MODEL slx_f09b170d5c8a
CONFIG AbsTol = auto
CONFIG FixedStep = 0.001
CONFIG MaxStep = auto
CONFIG MinStep = auto
CONFIG RelTol = 1e-3
CONFIG SampleTimeConstraint = Unconstrained
CONFIG Solver = ode5
CONFIG SolverMode = Auto
CONFIG SolverName = ode5
CONFIG StartTime = 0.0
CONFIG StopTime = 15
BLOCK [SubSystem] Control
  Ports = [3, 1]
  RequestExecContextInheritance = off
BLOCK [Constant] Control/Constant
  Value = a
BLOCK [Constant] Control/Constant1
  Value = d
BLOCK [SubSystem] Control/MATLAB Function
  ErrorFcn = Stateflow.Translate.translate
  PermitHierarchicalResolution = ExplicitOnly
  Ports = [4, 1]
  RequestExecContextInheritance = off
  SFBlockType = MATLAB Function
  TreatAsAtomicUnit = on
BLOCK [Demux] Control/MATLAB Function/ Demux 
  Outputs = 1
  Ports = [1, 1]
BLOCK [S-Function] Control/MATLAB Function/ SFunction 
  EnableBusSupport = on
  FunctionName = sf_sfun
  PortCounts = [4 2]
  Ports = [4, 2]
  Tag = Stateflow S-Function Static 2
BLOCK [Terminator] Control/MATLAB Function/ Terminator 
BLOCK [Outport] Control/MATLAB Function/K_inv
  IconDisplay = Port number
BLOCK [Inport] Control/MATLAB Function/a
  IconDisplay = Port number
  Port = 3
BLOCK [Inport] Control/MATLAB Function/beta
  IconDisplay = Port number
  Port = 2
BLOCK [Inport] Control/MATLAB Function/d
  IconDisplay = Port number
  Port = 4
BLOCK [Inport] Control/MATLAB Function/theta
  IconDisplay = Port number
BLOCK [Product] Control/Product
  InputSameDT = off
  Multiplication = Matrix(*)
  OutDataTypeStr = Inherit: Inherit via internal rule
  Ports = [2, 1]
  RndMeth = Floor
  SaturateOnIntegerOverflow = off
BLOCK [Inport] Control/W
  IconDisplay = Port number
BLOCK [Inport] Control/beta
  IconDisplay = Port number
  Port = 3
BLOCK [Inport] Control/theta
  IconDisplay = Port number
  Port = 2
BLOCK [Outport] Control/u
  IconDisplay = Port number
BLOCK [SubSystem] DKM
  Ports = [1, 4]
  RequestExecContextInheritance = off
BLOCK [Constant] DKM/Constant
  Value = r
BLOCK [Constant] DKM/Constant1
  Value = a
BLOCK [Demux] DKM/Demux1
  DisplayOption = bar
  Outputs = 2
  Ports = [1, 2]
BLOCK [Fcn] DKM/Fcn1
  Expr = sin(u)
BLOCK [Integrator] DKM/Integrator
  Ports = [1, 1]
BLOCK [Integrator] DKM/Integrator2
  InitialCondition = theta0
  Ports = [1, 1]
BLOCK [SubSystem] DKM/MATLAB Function2
  ErrorFcn = Stateflow.Translate.translate
  PermitHierarchicalResolution = ExplicitOnly
  Ports = [4, 2]
  RequestExecContextInheritance = off
  SFBlockType = MATLAB Function
  TreatAsAtomicUnit = on
BLOCK [Demux] DKM/MATLAB Function2/ Demux 
  Outputs = 1
  Ports = [1, 1]
BLOCK [S-Function] DKM/MATLAB Function2/ SFunction 
  EnableBusSupport = on
  FunctionName = sf_sfun
  PortCounts = [4 3]
  Ports = [4, 3]
  Tag = Stateflow S-Function Static 4
BLOCK [Terminator] DKM/MATLAB Function2/ Terminator 
BLOCK [Inport] DKM/MATLAB Function2/a
  IconDisplay = Port number
  Port = 2
BLOCK [Inport] DKM/MATLAB Function2/beta
  IconDisplay = Port number
  Port = 3
BLOCK [Inport] DKM/MATLAB Function2/theta
  IconDisplay = Port number
  Port = 4
BLOCK [Inport] DKM/MATLAB Function2/u_m
  IconDisplay = Port number
BLOCK [Outport] DKM/MATLAB Function2/x_dot
  IconDisplay = Port number
BLOCK [Outport] DKM/MATLAB Function2/y_dot
  IconDisplay = Port number
  Port = 2
BLOCK [Mux] DKM/Mux
  DisplayOption = bar
  Inputs = 2
  Ports = [2, 1]
BLOCK [Product] DKM/Product
  InputSameDT = off
  Inputs = **/
  OutDataTypeStr = Inherit: Inherit via internal rule
  Ports = [3, 1]
  RndMeth = Floor
  SaturateOnIntegerOverflow = off
BLOCK [Product] DKM/Product1
  InputSameDT = off
  OutDataTypeStr = Inherit: Inherit via internal rule
  Ports = [2, 1]
  RndMeth = Floor
  SaturateOnIntegerOverflow = off
BLOCK [ToWorkspace] DKM/To Workspace
  FixptAsFi = on
  MaxDataPoints = inf
  Ports = [1]
  SampleTime = -1
  Save2DSignal = 3-D array (concatenate along third dimension)
  VariableName = u
BLOCK [Outport] DKM/beta
  IconDisplay = Port number
  Port = 4
BLOCK [Inport] DKM/q_dot
  IconDisplay = Port number
BLOCK [Outport] DKM/theta
  IconDisplay = Port number
  Port = 3
BLOCK [Outport] DKM/x_dot
  IconDisplay = Port number
BLOCK [Outport] DKM/y_dot
  IconDisplay = Port number
  Port = 2
BLOCK [Gain] Gain
  Gain = K
  OutDataTypeStr = Inherit: Inherit via internal rule
  ParamDataTypeStr = Inherit: Inherit via internal rule
  SaturateOnIntegerOverflow = off
BLOCK [SubSystem] IKM
  Ports = [1, 1]
  RequestExecContextInheritance = off
BLOCK [Constant] IKM/Constant
  Value = a_e
BLOCK [Constant] IKM/Constant1
  Value = r_e
BLOCK [Demux] IKM/Demux
  DisplayOption = bar
  Outputs = 2
  Ports = [1, 2]
BLOCK [Mux] IKM/Mux
  DisplayOption = bar
  Inputs = 2
  Ports = [2, 1]
BLOCK [Product] IKM/Product
  InputSameDT = off
  Inputs = **/
  OutDataTypeStr = Inherit: Inherit via internal rule
  Ports = [3, 1]
  RndMeth = Floor
  SaturateOnIntegerOverflow = off
BLOCK [Outport] IKM/q_dot
  IconDisplay = Port number
BLOCK [Inport] IKM/u
  IconDisplay = Port number
BLOCK [SubSystem] Localization
  Ports = [4, 1]
  RequestExecContextInheritance = off
BLOCK [Constant] Localization/Constant1
  Value = a
BLOCK [Constant] Localization/Constant2
  Value = d
BLOCK [Integrator] Localization/Integrator2
  InitialCondition = x0
  Ports = [1, 1]
BLOCK [Integrator] Localization/Integrator3
  InitialCondition = y0
  Ports = [1, 1]
BLOCK [SubSystem] Localization/MATLAB Function1
  ErrorFcn = Stateflow.Translate.translate
  PermitHierarchicalResolution = ExplicitOnly
  Ports = [6, 1]
  RequestExecContextInheritance = off
  SFBlockType = MATLAB Function
  TreatAsAtomicUnit = on
BLOCK [Demux] Localization/MATLAB Function1/ Demux 
  Outputs = 1
  Ports = [1, 1]
BLOCK [S-Function] Localization/MATLAB Function1/ SFunction 
  EnableBusSupport = on
  FunctionName = sf_sfun
  PortCounts = [6 2]
  Ports = [6, 2]
  Tag = Stateflow S-Function Static 3
BLOCK [Terminator] Localization/MATLAB Function1/ Terminator 
BLOCK [Inport] Localization/MATLAB Function1/a
  IconDisplay = Port number
  Port = 6
BLOCK [Inport] Localization/MATLAB Function1/beta
  IconDisplay = Port number
  Port = 3
BLOCK [Inport] Localization/MATLAB Function1/d
  IconDisplay = Port number
  Port = 5
BLOCK [Outport] Localization/MATLAB Function1/h
  IconDisplay = Port number
BLOCK [Inport] Localization/MATLAB Function1/theta
  IconDisplay = Port number
  Port = 4
BLOCK [Inport] Localization/MATLAB Function1/x
  IconDisplay = Port number
BLOCK [Inport] Localization/MATLAB Function1/y
  IconDisplay = Port number
  Port = 2
BLOCK [Mux] Localization/Mux
  DisplayOption = bar
  Inputs = 2
  Ports = [2, 1]
BLOCK [ToWorkspace] Localization/To Workspace
  FixptAsFi = on
  MaxDataPoints = inf
  Ports = [1]
  SampleTime = -1
  Save2DSignal = 3-D array (concatenate along third dimension)
  VariableName = h
BLOCK [ToWorkspace] Localization/To Workspace1
  FixptAsFi = on
  MaxDataPoints = inf
  Ports = [1]
  SampleTime = -1
  Save2DSignal = 3-D array (concatenate along third dimension)
  VariableName = beta
BLOCK [Inport] Localization/beta
  IconDisplay = Port number
  Port = 4
BLOCK [Outport] Localization/h
  IconDisplay = Port number
BLOCK [Inport] Localization/theta
  IconDisplay = Port number
  Port = 3
BLOCK [Inport] Localization/x_dot
  IconDisplay = Port number
BLOCK [Inport] Localization/y_dot
  IconDisplay = Port number
  Port = 2
BLOCK [Mux] Mux
  DisplayOption = bar
  Inputs = 2
  Ports = [2, 1]
BLOCK [Mux] Mux1
  DisplayOption = bar
  Inputs = 2
  Ports = [2, 1]
BLOCK [Sum] Sum
  IconShape = round
  InputSameDT = off
  Inputs = -+|
  OutDataTypeStr = Inherit: Inherit via internal rule
  Ports = [2, 1]
  SaturateOnIntegerOverflow = off
BLOCK [Sum] Sum1
  IconShape = round
  InputSameDT = off
  Inputs = |++
  OutDataTypeStr = Inherit: Inherit via internal rule
  Ports = [2, 1]
  SaturateOnIntegerOverflow = off
BLOCK [ToWorkspace] To Workspace2
  FixptAsFi = on
  MaxDataPoints = inf
  Ports = [1]
  SampleTime = -1
  Save2DSignal = 3-D array (concatenate along third dimension)
  VariableName = error
BLOCK [SubSystem] Trajectory Generator
  Ports = [0, 4]
  RequestExecContextInheritance = off
BLOCK [Constant] Trajectory Generator/Constant
  Value = wd
BLOCK [Constant] Trajectory Generator/Constant1
  Value = R
BLOCK [Fcn] Trajectory Generator/Fcn
  Expr = u+pi/2
BLOCK [Integrator] Trajectory Generator/Integrator
  Ports = [1, 1]
BLOCK [Mux] Trajectory Generator/Mux
  DisplayOption = bar
  Inputs = 3
  Ports = [3, 1]
BLOCK [Mux] Trajectory Generator/Mux1
  DisplayOption = bar
  Inputs = 3
  Ports = [3, 1]
BLOCK [ToWorkspace] Trajectory Generator/To Workspace
  FixptAsFi = on
  MaxDataPoints = inf
  Ports = [1]
  SampleTime = -1
  Save2DSignal = 3-D array (concatenate along third dimension)
  VariableName = hd
BLOCK [Outport] Trajectory Generator/xd
  IconDisplay = Port number
BLOCK [Fcn] Trajectory Generator/xd Func
  Expr = u(3)*cos(u(2))
BLOCK [Outport] Trajectory Generator/xd_dot
  IconDisplay = Port number
  Port = 3
BLOCK [Fcn] Trajectory Generator/xd_dot Func
  Expr = -u(3)*u(1)*sin(u(2))
BLOCK [Outport] Trajectory Generator/yd
  IconDisplay = Port number
  Port = 2
BLOCK [Fcn] Trajectory Generator/yd Func
  Expr = u(3)*sin(u(2))
BLOCK [Outport] Trajectory Generator/yd_dot
  IconDisplay = Port number
  Port = 4
BLOCK [Fcn] Trajectory Generator/yd_dot Func
  Expr = u(3)*u(1)*cos(u(2))
LINE Control/Constant1:1 -> Control/MATLAB Function:4
LINE Control/Constant:1 -> Control/MATLAB Function:3
LINE Control/MATLAB Function:1 -> Control/Product:1
LINE Control/Product:1 -> Control/u:1
LINE Control/W:1 -> Control/Product:2
LINE Control/beta:1 -> Control/MATLAB Function:2
LINE Control/theta:1 -> Control/MATLAB Function:1
LINE Control:1 -> IKM:1
LINE DKM/Constant1:1 -> DKM/MATLAB Function2:2
LINE DKM/Constant1:1 -> DKM/Product:3
LINE DKM/Constant:1 -> DKM/Product:2
LINE DKM/Demux1:1 -> DKM/Product:1
LINE DKM/Demux1:2 -> DKM/Integrator:1
LINE DKM/Demux1:2 -> DKM/Mux:2
LINE DKM/Fcn1:1 -> DKM/Product1:2
LINE DKM/Integrator2:1 -> DKM/MATLAB Function2:4
LINE DKM/Integrator2:1 -> DKM/theta:1
LINE DKM/Integrator:1 -> DKM/Fcn1:1
LINE DKM/Integrator:1 -> DKM/MATLAB Function2:3
LINE DKM/Integrator:1 -> DKM/beta:1
LINE DKM/MATLAB Function2:1 -> DKM/x_dot:1
LINE DKM/MATLAB Function2:2 -> DKM/y_dot:1
LINE DKM/Mux:1 -> DKM/To Workspace:1
LINE DKM/Product1:1 -> DKM/Integrator2:1
LINE DKM/Product:1 -> DKM/MATLAB Function2:1
LINE DKM/Product:1 -> DKM/Mux:1
LINE DKM/Product:1 -> DKM/Product1:1
LINE DKM/q_dot:1 -> DKM/Demux1:1
LINE DKM:1 -> Localization:1
LINE DKM:2 -> Localization:2
LINE DKM:3 -> Control:2
LINE DKM:3 -> Localization:3
LINE DKM:4 -> Control:3
LINE DKM:4 -> Localization:4
LINE Gain:1 -> Sum1:1
LINE IKM/Constant1:1 -> IKM/Product:3
LINE IKM/Constant:1 -> IKM/Product:1
LINE IKM/Demux:1 -> IKM/Product:2
LINE IKM/Demux:2 -> IKM/Mux:2
LINE IKM/Mux:1 -> IKM/q_dot:1
LINE IKM/Product:1 -> IKM/Mux:1
LINE IKM/u:1 -> IKM/Demux:1
LINE IKM:1 -> DKM:1
LINE Localization/Constant1:1 -> Localization/MATLAB Function1:6
LINE Localization/Constant2:1 -> Localization/MATLAB Function1:5
LINE Localization/Integrator2:1 -> Localization/MATLAB Function1:1
LINE Localization/Integrator3:1 -> Localization/MATLAB Function1:2
LINE Localization/MATLAB Function1:1 -> Localization/Mux:1
LINE Localization/MATLAB Function1:1 -> Localization/h:1
LINE Localization/Mux:1 -> Localization/To Workspace:1
LINE Localization/beta:1 -> Localization/MATLAB Function1:3
LINE Localization/beta:1 -> Localization/To Workspace1:1
LINE Localization/theta:1 -> Localization/MATLAB Function1:4
LINE Localization/theta:1 -> Localization/Mux:2
LINE Localization/x_dot:1 -> Localization/Integrator2:1
LINE Localization/y_dot:1 -> Localization/Integrator3:1
LINE Localization:1 -> Sum:1
LINE Mux1:1 -> Sum1:2
LINE Mux:1 -> Sum:2
LINE Sum1:1 -> Control:1
LINE Sum:1 -> Gain:1
LINE Sum:1 -> To Workspace2:1
LINE Trajectory Generator/Constant1:1 -> Trajectory Generator/Mux:3
LINE Trajectory Generator/Constant:1 -> Trajectory Generator/Integrator:1
LINE Trajectory Generator/Constant:1 -> Trajectory Generator/Mux:1
LINE Trajectory Generator/Fcn:1 -> Trajectory Generator/Mux1:3
LINE Trajectory Generator/Integrator:1 -> Trajectory Generator/Fcn:1
LINE Trajectory Generator/Integrator:1 -> Trajectory Generator/Mux:2
LINE Trajectory Generator/Mux1:1 -> Trajectory Generator/To Workspace:1
LINE Trajectory Generator/Mux:1 -> Trajectory Generator/xd Func:1
LINE Trajectory Generator/Mux:1 -> Trajectory Generator/xd_dot Func:1
LINE Trajectory Generator/Mux:1 -> Trajectory Generator/yd Func:1
LINE Trajectory Generator/Mux:1 -> Trajectory Generator/yd_dot Func:1
LINE Trajectory Generator/xd Func:1 -> Trajectory Generator/Mux1:1
LINE Trajectory Generator/xd Func:1 -> Trajectory Generator/xd:1
LINE Trajectory Generator/xd_dot Func:1 -> Trajectory Generator/xd_dot:1
LINE Trajectory Generator/yd Func:1 -> Trajectory Generator/Mux1:2
LINE Trajectory Generator/yd Func:1 -> Trajectory Generator/yd:1
LINE Trajectory Generator/yd_dot Func:1 -> Trajectory Generator/yd_dot:1
LINE Trajectory Generator:1 -> Mux:1
LINE Trajectory Generator:2 -> Mux:2
LINE Trajectory Generator:3 -> Mux1:1
LINE Trajectory Generator:4 -> Mux1:2
CHART Control/MATLAB Function states=1 transitions=1
  STATE_LABEL 'eML_blk_kernel()'
  STATE_LABEL 'SCRIPT:\nfunction K_inv = Find_K_inv(theta,beta,a,d)\n%#codegen\n\nK = [a*cos(beta+theta)-d*sin(beta+theta)*sin(beta), -d*sin(beta+theta);...\n     a*sin(beta+theta)+d*cos(beta+theta)*sin(beta), d*cos(beta+theta)];\n \n K_inv = inv(K);'
CHART Localization/MATLAB Function1 states=1 transitions=1
  STATE_LABEL 'eML_blk_kernel()'
  STATE_LABEL 'SCRIPT:\nfunction h = Find_h(x,y,beta,theta,d,a)\n%#codegen\nz1 = x + a*cos(theta) + d*cos(theta+beta);\nz2 = y + a*sin(theta) + d*sin(theta+beta);\nh = [z1;z2];\n'
CHART DKM/MATLAB Function2 states=1 transitions=1
  STATE_LABEL 'eML_blk_kernel()'
  STATE_LABEL 'SCRIPT:\nfunction [x_dot,y_dot] = Find_xy_dot(u_m,a,beta,theta)\n\nx_dot = a*cos(beta)*cos(theta)*u_m;\ny_dot = a*cos(beta)*sin(theta)*u_m;\n'
